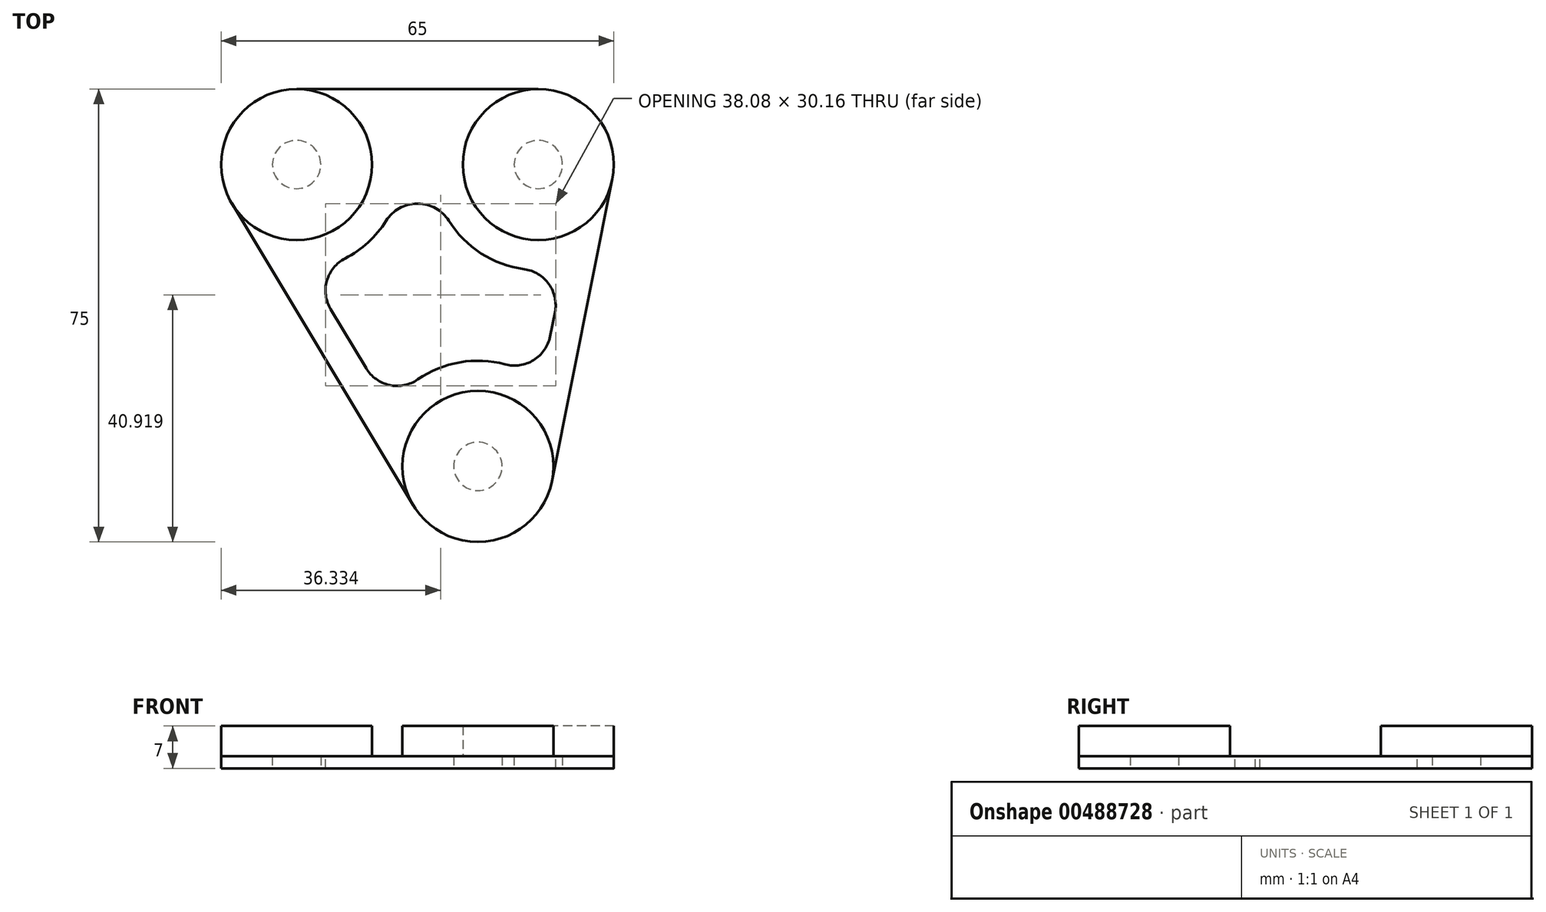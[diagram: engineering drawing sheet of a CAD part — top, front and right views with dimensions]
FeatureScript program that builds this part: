
annotation { "Feature Type Name" : "Feature", "Feature Type Description" : "" }
export const myFeature = defineFeature(function(context is Context, id is Id, definition is map)
    precondition{}
    {
        {
            var Q0;
            Q0=qCreatedBy(makeId("Top.planeOp"),FACE);
            var sketch = newSketch(context, id + "F0", { "sketchPlane" : qUnion([Q0])});
            skCircle(sketch, "E0", {"center": v(-20, 20) * mm, "radius": 4 * mm});
            skCircle(sketch, "E1", {"center": v(20, 20) * mm, "radius": 4 * mm});
            skCircle(sketch, "E2", {"center": v(10, -30) * mm, "radius": 4 * mm});
            skCircle(sketch, "E3", {"center": v(-20, 20) * mm, "radius": 12.5 * mm});
            skCircle(sketch, "E4", {"center": v(20, 20) * mm, "radius": 12.5 * mm});
            skCircle(sketch, "E5", {"center": v(10, -30) * mm, "radius": 12.5 * mm});
            skLineSegment(sketch, "E6", {"start": v(-30.72, 13.57) * mm, "end": v(-0.72, -36.43) * mm});
            skLineSegment(sketch, "E7", {"start": v(-20, 32.5) * mm, "end": v(20, 32.5) * mm});
            skLineSegment(sketch, "E8.trimOffspring", {"start": v(32.26, 17.55) * mm, "end": v(22.26, -32.45) * mm});
            skLineSegment(sketch, "E9", {"start": v(-27.08, 7.5) * mm, "end": v(30.25, 7.5) * mm});
            skLineSegment(sketch, "E10.0", {"start": v(-13.7, -5.07) * mm, "end": v(-11, -9.59) * mm});
            skLineSegment(sketch, "E11.0", {"start": v(22.95, -3.48) * mm, "end": v(22.11, -7.68) * mm});
            skLineSegment(sketch, "E12.0", {"start": v(-9.42, 2.5) * mm, "end": v(18.05, 2.5) * mm});
            skLineSegment(sketch, "E13", {"start": v(-38.72, -17.5) * mm, "end": v(46.95, -17.5) * mm});
            skLineSegment(sketch, "E14.0", {"start": v(-5.85, -12.5) * mm, "end": v(16.23, -12.5) * mm});
            skArc(sketch, "E15.filletArc", {"start": v(-9.42, 2.5) * mm, "mid": v(-13.77, -0.04) * mm, "end": v(-13.7, -5.07) * mm});
            skArc(sketch, "E16.filletArc", {"start": v(22.95, -3.48) * mm, "mid": v(21.92, 0.67) * mm, "end": v(18.05, 2.5) * mm});
            skArc(sketch, "E17.filletArc", {"start": v(-11, -9.59) * mm, "mid": v(-8.8, -11.72) * mm, "end": v(-5.85, -12.5) * mm});
            skArc(sketch, "E18.filletArc", {"start": v(16.23, -12.5) * mm, "mid": v(20.03, -11.14) * mm, "end": v(22.11, -7.68) * mm});
            skSolve(sketch);
        }
        {
            var Q0;
            Q0=makeQuery(id+"F0.imprint","IMPRINT",FACE,{"disambiguationData":[TD([[makeQuery(id+"F0.imprint","IMPRINT",EDGE,{"derivedFrom":sQuery(id+"F0.wireOp",EDGE,"E0")}),-1.0]])]});
            var Q1;
            Q1=makeQuery(id+"F0.imprint","IMPRINT",FACE,{"disambiguationData":[TD([[makeQuery(id+"F0.imprint","IMPRINT",EDGE,{"derivedFrom":sQuery(id+"F0.wireOp",EDGE,"E1")}),-1.0]])]});
            var Q2;
            {var subQ0=sQuery(id+"F0.wireOp",EDGE,"E7");Q2=makeQuery(id+"F0.imprint","IMPRINT",FACE,{"disambiguationData":[TD([[makeQuery(id+"F0.imprint","IMPRINT",EDGE,{"derivedFrom":subQ0}),-1.0]])]});}
            var Q3;
            {var subQ0=sQuery(id+"F0.wireOp",EDGE,"E8.trimOffspring");var subQ1=sQuery(id+"F0.wireOp",EDGE,"E4");var subQ2=makeQuery(id+"F0.imprint","INTERSECT",VERTEX,{"derivedFrom":[subQ1,subQ0]});Q3=makeQuery(id+"F0.imprint","IMPRINT",FACE,{"disambiguationData":[TD([[makeQuery(id+"F0.imprint","IMPRINT",EDGE,{"disambiguationData":[TD([[subQ2,1.0]])],"derivedFrom":subQ1}),-1.0]])]});}
            var Q4;
            {var subQ0=sQuery(id+"F0.wireOp",EDGE,"E6");var subQ1=sQuery(id+"F0.wireOp",EDGE,"E3");var subQ2=makeQuery(id+"F0.imprint","INTERSECT",VERTEX,{"derivedFrom":[subQ1,subQ0]});Q4=makeQuery(id+"F0.imprint","IMPRINT",FACE,{"disambiguationData":[TD([[makeQuery(id+"F0.imprint","IMPRINT",EDGE,{"disambiguationData":[TD([[subQ2,-1.0]])],"derivedFrom":subQ1}),-1.0]])]});}
            var Q5;
            Q5=makeQuery(id+"F0.imprint","IMPRINT",FACE,{"disambiguationData":[TD([[makeQuery(id+"F0.imprint","IMPRINT",EDGE,{"derivedFrom":sQuery(id+"F0.wireOp",EDGE,"E10.0")}),-1.0]])]});
            var Q6;
            {var subQ0=sQuery(id+"F0.wireOp",EDGE,"E8.trimOffspring");var subQ1=sQuery(id+"F0.wireOp",EDGE,"E5");var subQ2=makeQuery(id+"F0.imprint","INTERSECT",VERTEX,{"derivedFrom":[subQ1,subQ0]});Q6=makeQuery(id+"F0.imprint","IMPRINT",FACE,{"disambiguationData":[TD([[makeQuery(id+"F0.imprint","IMPRINT",EDGE,{"disambiguationData":[TD([[subQ2,-1.0]])],"derivedFrom":subQ1}),-1.0]])]});}
            var Q7;
            {var subQ0=sQuery(id+"F0.wireOp",EDGE,"E6");var subQ1=sQuery(id+"F0.wireOp",EDGE,"E5");var subQ2=makeQuery(id+"F0.imprint","INTERSECT",VERTEX,{"derivedFrom":[subQ1,subQ0]});Q7=makeQuery(id+"F0.imprint","IMPRINT",FACE,{"disambiguationData":[TD([[makeQuery(id+"F0.imprint","IMPRINT",EDGE,{"disambiguationData":[TD([[subQ2,1.0]])],"derivedFrom":subQ1}),-1.0]])]});}
            var Q8;
            Q8=makeQuery(id+"F0.imprint","IMPRINT",FACE,{"disambiguationData":[TD([[makeQuery(id+"F0.imprint","IMPRINT",EDGE,{"derivedFrom":sQuery(id+"F0.wireOp",EDGE,"E2")}),-1.0]])]});
            var Q9;
            Q9=makeQuery(id+"F0.imprint","IMPRINT",FACE,{"disambiguationData":[TD([[makeQuery(id+"F0.imprint","IMPRINT",EDGE,{"derivedFrom":sQuery(id+"F0.wireOp",EDGE,"E10.0")}),1.0]])]});
            extrude(context, id + "F1", {"entities" : qUnion([Q0, Q1, Q2, Q3, Q4, Q5, Q6, Q7, Q8, Q9]), "depth" : 2 * mm});
        }
        {
            var Q0;
            Q0=makeQuery(id+"F1.opExtrude","CAP_FACE",FACE,{"disambiguationData":[OSD([sQuery(id+"F0.wireOp",EDGE,"E0"),sQuery(id+"F0.wireOp",EDGE,"E1"),sQuery(id+"F0.wireOp",EDGE,"E2"),sQuery(id+"F0.wireOp",EDGE,"E3"),sQuery(id+"F0.wireOp",EDGE,"E4"),sQuery(id+"F0.wireOp",EDGE,"E5"),sQuery(id+"F0.wireOp",EDGE,"E6"),sQuery(id+"F0.wireOp",EDGE,"E7"),sQuery(id+"F0.wireOp",EDGE,"E8.trimOffspring"),sQuery(id+"F0.wireOp",EDGE,"E10.0"),sQuery(id+"F0.wireOp",EDGE,"E11.0"),sQuery(id+"F0.wireOp",EDGE,"E12.0"),sQuery(id+"F0.wireOp",EDGE,"E14.0"),sQuery(id+"F0.wireOp",EDGE,"E15.filletArc"),sQuery(id+"F0.wireOp",EDGE,"E16.filletArc"),sQuery(id+"F0.wireOp",EDGE,"E17.filletArc"),sQuery(id+"F0.wireOp",EDGE,"E18.filletArc")])],"isStart":false});
            var sketch = newSketch(context, id + "F2", { "sketchPlane" : qUnion([Q0])});
            skCircle(sketch, "E19", {"center": v(-20, 20) * mm, "radius": 12.5 * mm});
            skCircle(sketch, "E20", {"center": v(20, 20) * mm, "radius": 12.5 * mm});
            skCircle(sketch, "E21", {"center": v(10, -30) * mm, "radius": 12.5 * mm});
            skSolve(sketch);
        }
        {
            var Q0;
            Q0 = qSketchRegion(id + "F2", true);
            extrude(context, id + "F3", {"entities" : qUnion([Q0]), "depth" : 5 * mm});
        }
        {
            var Q0;
            Q0=makeQuery(id+"F1.opExtrude","CAP_FACE",FACE,{"disambiguationData":[OSD([sQuery(id+"F0.wireOp",EDGE,"E0"),sQuery(id+"F0.wireOp",EDGE,"E1"),sQuery(id+"F0.wireOp",EDGE,"E2"),sQuery(id+"F0.wireOp",EDGE,"E3"),sQuery(id+"F0.wireOp",EDGE,"E4"),sQuery(id+"F0.wireOp",EDGE,"E5"),sQuery(id+"F0.wireOp",EDGE,"E6"),sQuery(id+"F0.wireOp",EDGE,"E7"),sQuery(id+"F0.wireOp",EDGE,"E8.trimOffspring")])],"isStart":false});
            var sketch = newSketch(context, id + "F4", { "sketchPlane" : qUnion([Q0])});
            skArc(sketch, "E22", {"start": v(-11.97, 4.45) * mm, "mid": v(-8.16, 7.12) * mm, "end": v(-5.18, 10.7) * mm});
            skArc(sketch, "E23", {"start": v(5.18, 10.7) * mm, "mid": v(10.53, 5.28) * mm, "end": v(17.67, 2.66) * mm});
            skArc(sketch, "E24", {"start": v(14.52, -13.1) * mm, "mid": v(7.01, -12.76) * mm, "end": v(0.06, -15.6) * mm});
            skCircle(sketch, "E25.0", {"center": v(10, -30) * mm, "radius": 12.5 * mm});
            skCircle(sketch, "E26.0", {"center": v(-20, 20) * mm, "radius": 12.5 * mm});
            skCircle(sketch, "E27.0.0", {"center": v(20, 20) * mm, "radius": 12.5 * mm});
            skLineSegment(sketch, "E28.0", {"start": v(-30.72, 13.57) * mm, "end": v(-0.72, -36.43) * mm});
            skLineSegment(sketch, "E29.0", {"start": v(32.26, 17.55) * mm, "end": v(22.26, -32.45) * mm});
            skLineSegment(sketch, "E30.0", {"start": v(-26.43, 16.14) * mm, "end": v(-21.29, 7.57) * mm});
            skLineSegment(sketch, "E31.0", {"start": v(22.76, -4.47) * mm, "end": v(21.95, -8.47) * mm});
            skLineSegment(sketch, "E32", {"start": v(-0.1, 13.5) * mm, "end": v(0.1, 13.5) * mm});
            skArc(sketch, "E33.filletArc", {"start": v(-0.1, 13.5) * mm, "mid": v(-3, 12.75) * mm, "end": v(-5.18, 10.7) * mm});
            skArc(sketch, "E34.filletArc", {"start": v(5.18, 10.7) * mm, "mid": v(3, 12.75) * mm, "end": v(0.1, 13.5) * mm});
            skArc(sketch, "E35.filletArc", {"start": v(22.76, -4.47) * mm, "mid": v(21.76, 0.2) * mm, "end": v(17.67, 2.66) * mm});
            skLineSegment(sketch, "E36.trimOffspring", {"start": v(-1.58, -25.28) * mm, "end": v(3.57, -33.86) * mm});
            skLineSegment(sketch, "E37.trimOffspring", {"start": v(19.32, -21.67) * mm, "end": v(17.35, -31.47) * mm});
            skLineSegment(sketch, "E38.trimOffspring", {"start": v(-14.37, -3.97) * mm, "end": v(-8.5, -13.75) * mm});
            skArc(sketch, "E39.filletArc", {"start": v(-11.97, 4.45) * mm, "mid": v(-15, 0.76) * mm, "end": v(-14.37, -3.97) * mm});
            skPoint(sketch, "E40.visualSharp", {"position": v(-4.57, -20.3) * mm});
            skArc(sketch, "E40.filletArc", {"start": v(-8.5, -13.75) * mm, "mid": v(-4.62, -16.53) * mm, "end": v(0.06, -15.6) * mm});
            skArc(sketch, "E41.filletArc", {"start": v(14.52, -13.1) * mm, "mid": v(19.24, -12.4) * mm, "end": v(21.95, -8.47) * mm});
            skSolve(sketch);
        }
        {
            var Q0;
            Q0=makeQuery(id+"F4.imprint","IMPRINT",FACE,{"disambiguationData":[TD([[makeQuery(id+"F4.imprint","IMPRINT",EDGE,{"derivedFrom":sQuery(id+"F4.wireOp",EDGE,"E22")}),-1.0]])]});
            extrude(context, id + "F5", {"entities" : qUnion([Q0]), "operationType" : NewBodyOperationType.REMOVE, "oppositeDirection" : true, "depth" : 25 * mm});
        }
    });
